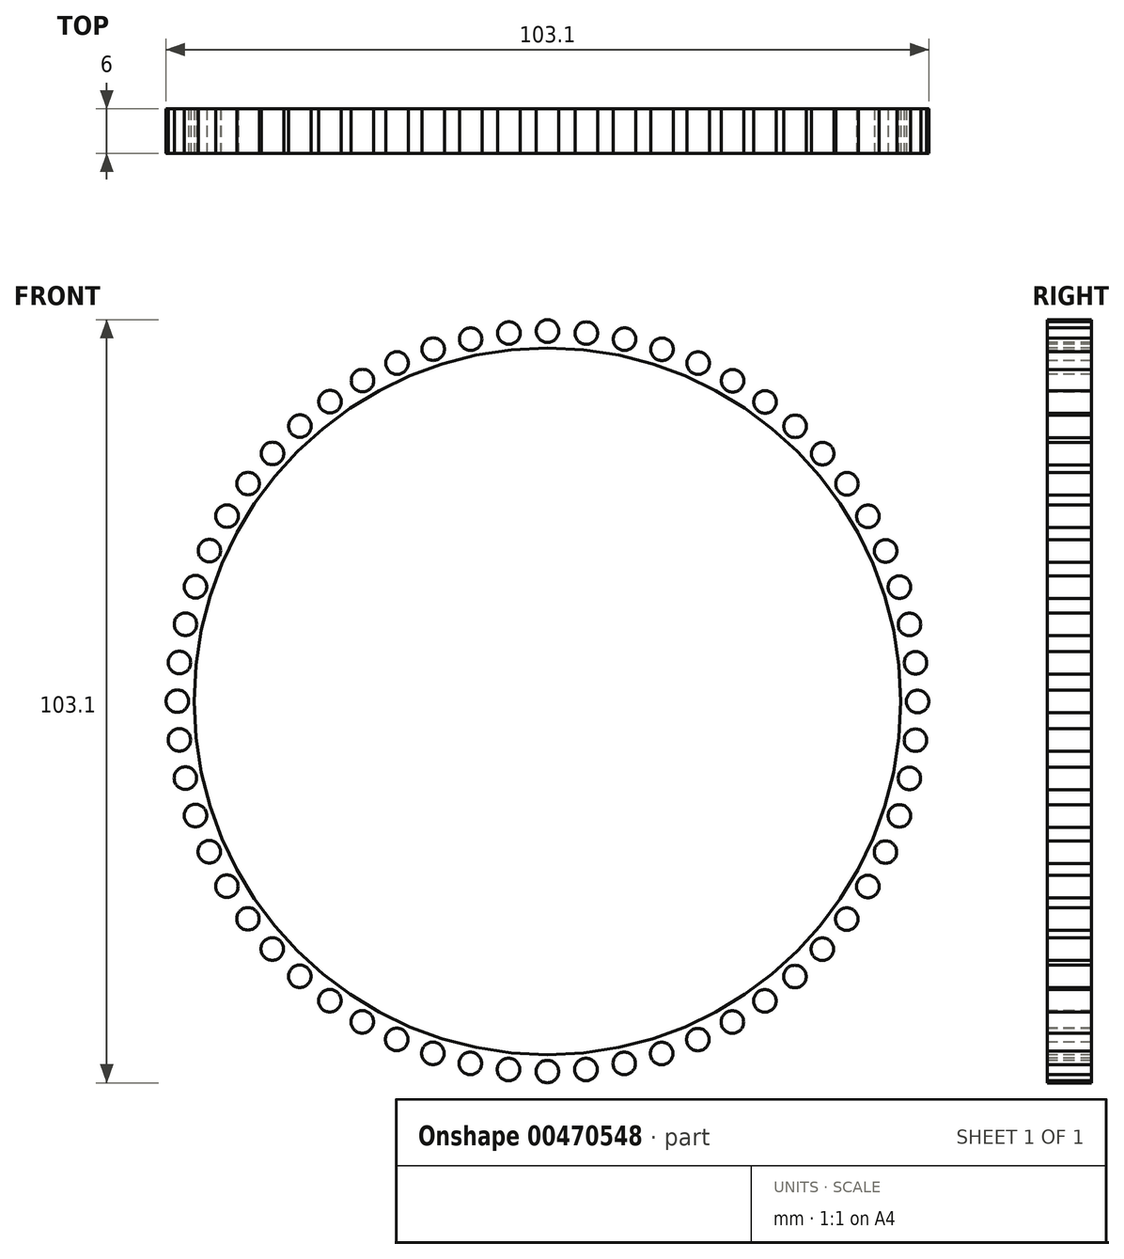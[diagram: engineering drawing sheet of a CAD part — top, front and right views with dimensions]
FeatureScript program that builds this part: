
annotation { "Feature Type Name" : "Feature", "Feature Type Description" : "" }
export const myFeature = defineFeature(function(context is Context, id is Id, definition is map)
    precondition{}
    {
        {
            var Q0;
            Q0=qCreatedBy(makeId("Front.planeOp"),FACE);
            var sketch = newSketch(context, id + "F0", { "sketchPlane" : qUnion([Q0])});
            skCircle(sketch, "E0", {"center": v(0, 0) * mm, "radius": 47.75 * mm});
            skCircle(sketch, "E1", {"center": v(0, 0) * mm, "radius": 49.8 * mm, "construction": true});
            skCircle(sketch, "E2", {"center": v(0, 0) * mm, "radius": 51.55 * mm, "construction": true});
            skLineSegment(sketch, "E3", {"start": v(0, 0) * mm, "end": v(0, 63.2) * mm, "construction": true});
            skLineSegment(sketch, "E4", {"start": v(0, 0) * mm, "end": v(-5.54, 63.36) * mm, "construction": true});
            skCircle(sketch, "E5", {"center": v(0.02, 50.02) * mm, "radius": 1.52 * mm});
            skPoint(sketch, "E5.first.point", {"position": v(0, 51.55) * mm});
            skPoint(sketch, "E5.second.point", {"position": v(0, 48.5) * mm});
            skPoint(sketch, "E5.third.point", {"position": v(1.53, 49.78) * mm});
            skSolve(sketch);
        }
        {
            var Q0;
            Q0=sQuery(id+"F0.wireOp",EDGE,"E5");
            var Q1;
            Q1=sQuery(id+"F0.wireOp",EDGE,"E0");
            extrude(context, id + "F1", {"bodyType" : ToolBodyType.SURFACE, "surfaceEntities" : qUnion([Q0, Q1]), "depth" : 6 * mm});
        }
        {
            var Q0;
            Q0=makeQuery(id+"F1.opExtrude","SWEPT_BODY",BODY,{"disambiguationData":[OSD([sQuery(id+"F0.wireOp",EDGE,"E5")])]});
            var Q1;
            Q1=makeQuery(id+"F1.opExtrude","CAP_EDGE",EDGE,{"disambiguationData":[OSD([sQuery(id+"F0.wireOp",EDGE,"E0")])],"isStart":true});
            circularPattern(context, id + "F2", {"entities" : qUnion([Q0]), "axis" : qUnion([Q1]), "angle" : 360 * degree, "instanceCount" : 60, "equalSpace" : true});
        }
    });
